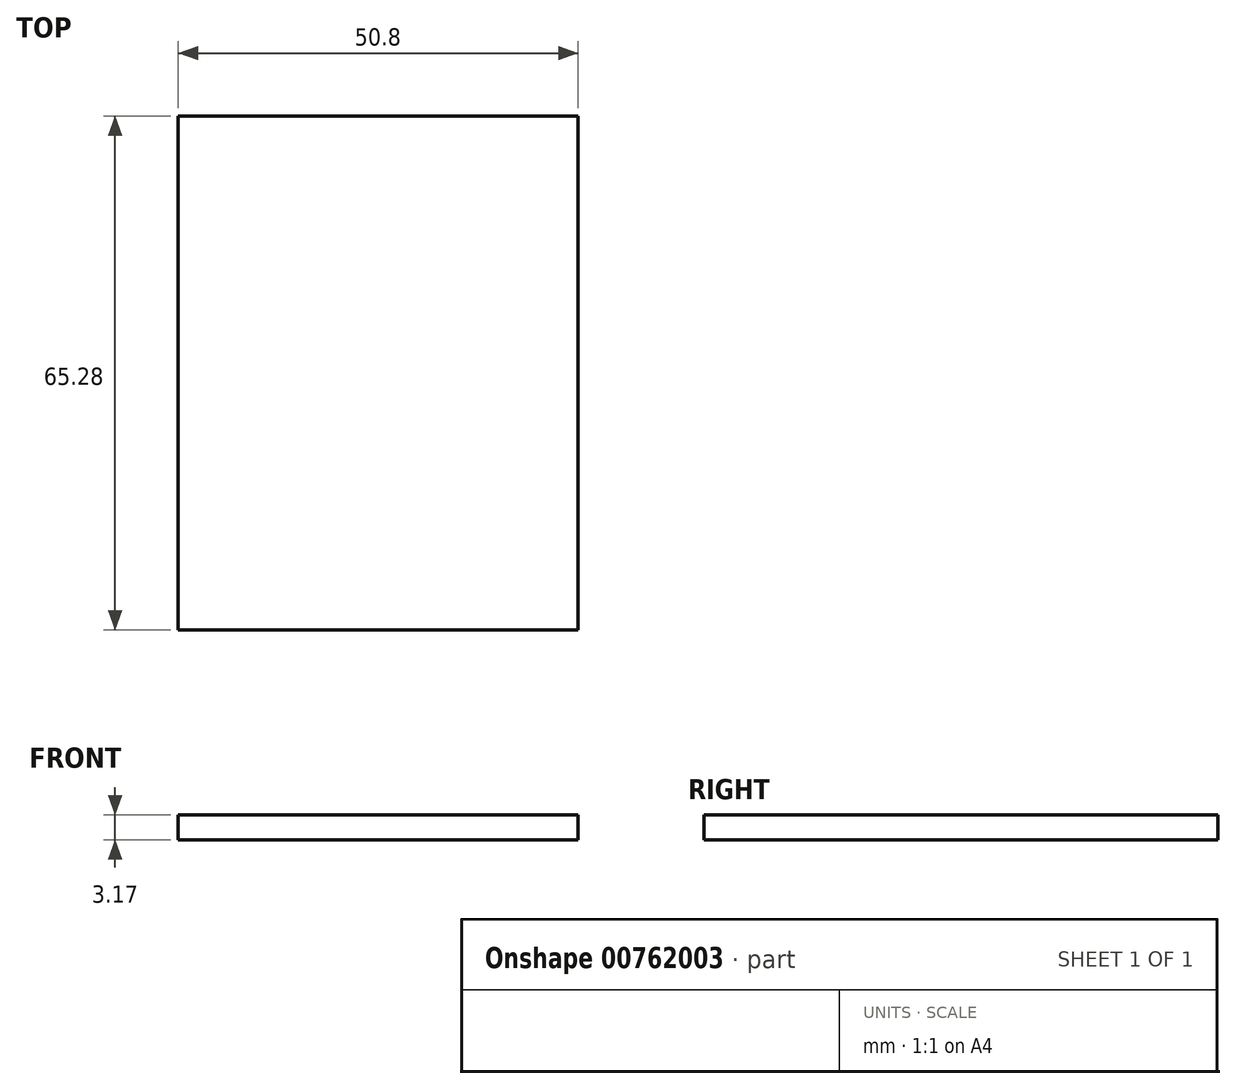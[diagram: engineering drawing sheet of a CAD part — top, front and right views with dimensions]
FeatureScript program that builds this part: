
annotation { "Feature Type Name" : "Feature", "Feature Type Description" : "" }
export const myFeature = defineFeature(function(context is Context, id is Id, definition is map)
    precondition{}
    {
        {
            var Q0;
            Q0=qCreatedBy(makeId("Top.planeOp"),FACE);
            var sketch = newSketch(context, id + "F0", { "sketchPlane" : qUnion([Q0])});
            skLineSegment(sketch, "E0", {"start": v(-35.4, 33.45) * mm, "end": v(-35.4, -31.83) * mm});
            skLineSegment(sketch, "E1", {"start": v(-35.4, 33.45) * mm, "end": v(15.4, 33.45) * mm});
            skLineSegment(sketch, "E2", {"start": v(-35.4, -31.83) * mm, "end": v(15.4, -31.83) * mm});
            skLineSegment(sketch, "E3", {"start": v(15.4, 33.45) * mm, "end": v(15.4, -31.83) * mm});
            skSolve(sketch);
        }
        {
            var Q0;
            Q0=makeQuery(id+"F0.imprint","IMPRINT",FACE,{"disambiguationData":[TD([[makeQuery(id+"F0.imprint","IMPRINT",EDGE,{"derivedFrom":sQuery(id+"F0.wireOp",EDGE,"E0")}),1.0]])]});
            extrude(context, id + "F1", {"entities" : qUnion([Q0]), "depth" : 3.17 * mm, "offsetDistance" : 25.4 * mm});
        }
    });
